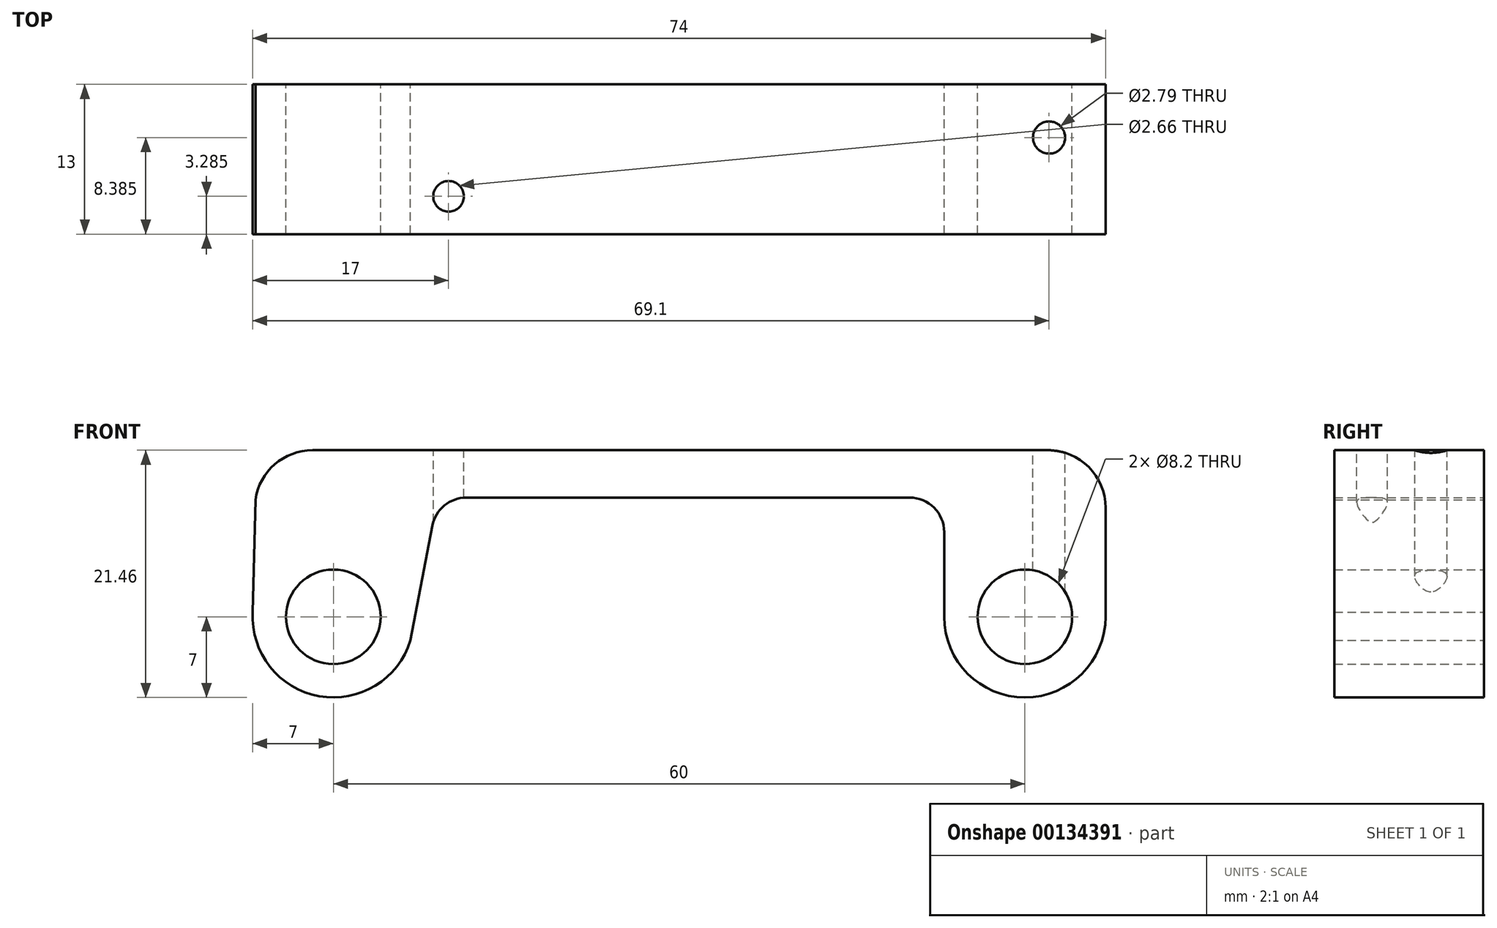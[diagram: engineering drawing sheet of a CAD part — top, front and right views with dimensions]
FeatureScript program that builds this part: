
annotation { "Feature Type Name" : "Feature", "Feature Type Description" : "" }
export const myFeature = defineFeature(function(context is Context, id is Id, definition is map)
    precondition{}
    {
        {
            var Q0;
            Q0=qCreatedBy(makeId("Front.planeOp"),FACE);
            var sketch = newSketch(context, id + "F0", { "sketchPlane" : qUnion([Q0])});
            skCircle(sketch, "E0", {"center": v(-30, 0) * mm, "radius": 4.1 * mm});
            skArc(sketch, "E1", {"start": v(-36.99, 0.4) * mm, "mid": v(-31.23, -6.9) * mm, "end": v(-23.3, -2.04) * mm});
            skArc(sketch, "E2.MirrorC", {"start": v(37, 0) * mm, "mid": v(30, -7) * mm, "end": v(23, 0) * mm});
            skCircle(sketch, "E3.MirrorC", {"center": v(30, 0) * mm, "radius": 4.1 * mm});
            skLineSegment(sketch, "E4.bottom", {"start": v(-31.8, 14.46) * mm, "end": v(1.21, 14.46) * mm});
            skLineSegment(sketch, "E5.MirrorCS", {"start": v(32, 14.46) * mm, "end": v(-1.21, 14.46) * mm});
            skLineSegment(sketch, "E6", {"start": v(37, 9.46) * mm, "end": v(37, 0) * mm});
            skLineSegment(sketch, "E7", {"start": v(-23.3, -2.04) * mm, "end": v(-21.4, 7.9) * mm});
            skLineSegment(sketch, "E8", {"start": v(23, 0) * mm, "end": v(23, 7.35) * mm});
            skLineSegment(sketch, "E9.trimOffspring", {"start": v(-18.45, 10.35) * mm, "end": v(-9.23, 10.35) * mm});
            skLineSegment(sketch, "E10.trimOffspring", {"start": v(20, 10.35) * mm, "end": v(10, 10.35) * mm});
            skArc(sketch, "E11.filletArc", {"start": v(-31.8, 14.46) * mm, "mid": v(-35.09, 13.23) * mm, "end": v(-36.76, 10.15) * mm});
            skArc(sketch, "E12.filletArc", {"start": v(37, 9.46) * mm, "mid": v(35.54, 13) * mm, "end": v(32, 14.46) * mm});
            skPoint(sketch, "E13.visualSharp", {"position": v(23, 10.35) * mm});
            skArc(sketch, "E13.filletArc", {"start": v(23, 7.35) * mm, "mid": v(22.12, 9.47) * mm, "end": v(20, 10.35) * mm});
            skPoint(sketch, "E14.visualSharp", {"position": v(-20.93, 10.35) * mm});
            skArc(sketch, "E14.filletArc", {"start": v(-18.45, 10.35) * mm, "mid": v(-20.37, 9.66) * mm, "end": v(-21.4, 7.9) * mm});
            skPoint(sketch, "E15.end.orphan", {"position": v(-36.26, 0) * mm});
            skLineSegment(sketch, "E16", {"start": v(-36.76, 10.15) * mm, "end": v(-36.99, 0.4) * mm});
            skLineSegment(sketch, "E17", {"start": v(-9.23, 10.35) * mm, "end": v(0, 10.35) * mm});
            skLineSegment(sketch, "E18", {"start": v(10, 10.35) * mm, "end": v(0, 10.35) * mm});
            skSolve(sketch);
        }
        {
            var Q0;
            Q0=qSketchRegion(id+"F0",true);
            extrude(context, id + "F1", {"entities" : qUnion([Q0]), "depth" : 13 * mm});
        }
        {
            var Q0;
            Q0=makeQuery(id+"F1.opExtrude","SWEPT_FACE",FACE,{"disambiguationData":[OSD([sQuery(id+"F0.wireOp",EDGE,"E4.bottom"),sQuery(id+"F0.wireOp",EDGE,"E5.MirrorCS")])]});
            var sketch = newSketch(context, id + "F2", { "sketchPlane" : qUnion([Q0])});
            skCircle(sketch, "E19", {"center": v(-20, -9.72) * mm, "radius": 1.33 * mm});
            skCircle(sketch, "E20", {"center": v(32.1, -4.62) * mm, "radius": 1.4 * mm});
            skSolve(sketch);
        }
        {
            var Q0;
            Q0=qSketchRegion(id+"F2",true);
            extrude(context, id + "F3", {"entities" : qUnion([Q0]), "operationType" : NewBodyOperationType.REMOVE, "oppositeDirection" : true, "depth" : 15 * mm});
        }
    });
